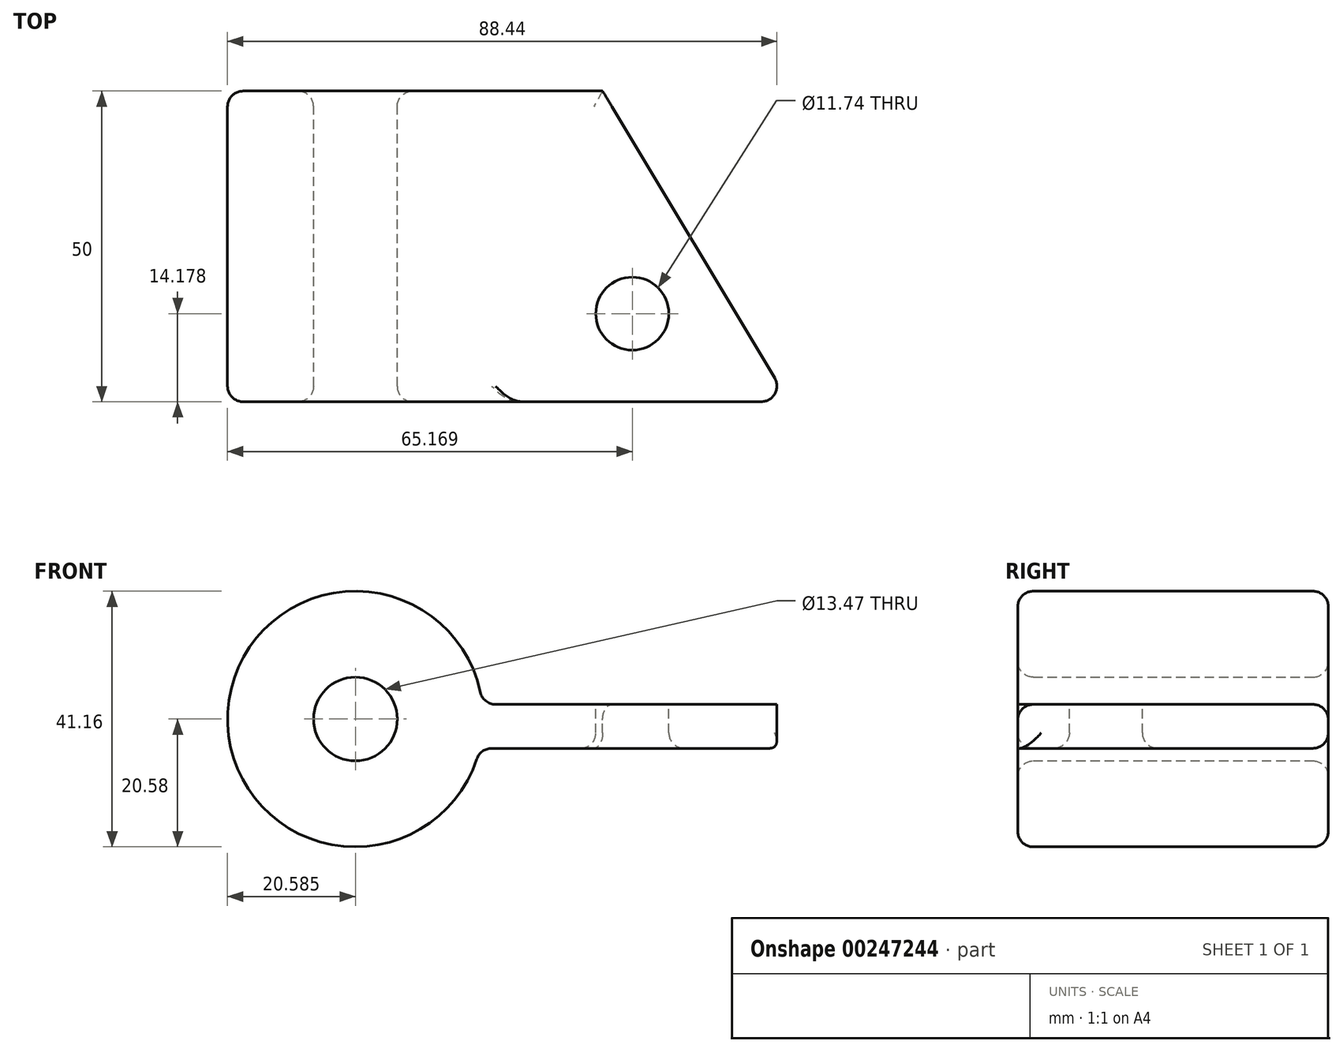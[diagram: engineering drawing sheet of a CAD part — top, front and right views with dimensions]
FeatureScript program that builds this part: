
annotation { "Feature Type Name" : "Feature", "Feature Type Description" : "" }
export const myFeature = defineFeature(function(context is Context, id is Id, definition is map)
    precondition{}
    {
        {
            var Q0;
            Q0=qCreatedBy(makeId("Front.planeOp"),FACE);
            var sketch = newSketch(context, id + "F0", { "sketchPlane" : qUnion([Q0])});
            skCircle(sketch, "E0", {"center": v(-44.76, 6.82) * mm, "radius": 20.58 * mm});
            skCircle(sketch, "E1", {"center": v(-44.76, 6.82) * mm, "radius": 6.74 * mm});
            skSolve(sketch);
        }
        {
            var Q0;
            Q0=makeQuery(id+"F0.imprint","IMPRINT",FACE,{"disambiguationData":[TD([[makeQuery(id+"F0.imprint","IMPRINT",EDGE,{"derivedFrom":sQuery(id+"F0.wireOp",EDGE,"E0")}),1.0]])]});
            extrude(context, id + "F1", {"entities" : qUnion([Q0]), "depth" : 50 * mm});
        }
        {
            var Q0;
            Q0=qCreatedBy(makeId("Right.planeOp"),FACE);
            var sketch = newSketch(context, id + "F2", { "sketchPlane" : qUnion([Q0])});
            skLineSegment(sketch, "E2.bottom", {"start": v(-50.14, 9.18) * mm, "end": v(0, 9.18) * mm});
            skLineSegment(sketch, "E2.top", {"start": v(-50.14, 2.1) * mm, "end": v(0, 2.1) * mm});
            skLineSegment(sketch, "E2.left", {"start": v(-50.14, 9.18) * mm, "end": v(-50.14, 2.1) * mm});
            skLineSegment(sketch, "E2.right", {"start": v(0, 9.18) * mm, "end": v(0, 2.1) * mm});
            skSolve(sketch);
        }
        {
            var Q0;
            Q0=makeQuery(id+"F2.imprint","IMPRINT",FACE,{"disambiguationData":[TD([[makeQuery(id+"F2.imprint","IMPRINT",EDGE,{"derivedFrom":sQuery(id+"F2.wireOp",EDGE,"E2.bottom")}),-1.0]])]});
            extrude(context, id + "F3", {"entities" : qUnion([Q0]), "oppositeDirection" : true, "depth" : 25 * mm});
        }
        {
            var Q0;
            Q0=makeQuery(id+"F3.opExtrude","SWEPT_BODY",BODY,{"disambiguationData":[OSD([sQuery(id+"F2.wireOp",EDGE,"E2.bottom"),sQuery(id+"F2.wireOp",EDGE,"E2.top"),sQuery(id+"F2.wireOp",EDGE,"E2.left"),sQuery(id+"F2.wireOp",EDGE,"E2.right")])]});
            var Q1;
            Q1=makeQuery(id+"F1.opExtrude","SWEPT_BODY",BODY,{"disambiguationData":[OSD([sQuery(id+"F0.wireOp",EDGE,"E0"),sQuery(id+"F0.wireOp",EDGE,"E1")])]});
            booleanBodies(context, id + "F4", {"operationType" : BooleanOperationType.UNION, "tools" : qUnion([Q0, Q1])});
        }
        {
            var Q0;
            Q0=makeQuery(id+"F3.opExtrude","CAP_FACE",FACE,{"disambiguationData":[OSD([sQuery(id+"F2.wireOp",EDGE,"E2.bottom"),sQuery(id+"F2.wireOp",EDGE,"E2.top"),sQuery(id+"F2.wireOp",EDGE,"E2.left"),sQuery(id+"F2.wireOp",EDGE,"E2.right")])],"isStart":true});
            extrude(context, id + "F5", {"entities" : qUnion([Q0]), "operationType" : NewBodyOperationType.ADD, "depth" : 25 * mm});
        }
        {
            var Q0;
            {var subQ0=sQuery(id+"F2.wireOp",EDGE,"E2.left");Q0=makeQuery(id+"F5.boolean.opBoolean","MERGE",FACE,{"derivedFrom":[makeQuery(id+"F3.opExtrude","SWEPT_FACE",FACE,{"disambiguationData":[OSD([subQ0])]}),makeQuery(id+"F5.opExtrude","SWEPT_FACE",FACE,{"disambiguationData":[OSD([subQ0])]})]});}
            var Q1;
            Q1=makeQuery(id+"F1.opExtrude","CAP_FACE",FACE,{"disambiguationData":[OSD([sQuery(id+"F0.wireOp",EDGE,"E0"),sQuery(id+"F0.wireOp",EDGE,"E1")])],"isStart":false});
            extrude(context, id + "F6", {"entities" : qUnion([Q0]), "operationType" : NewBodyOperationType.REMOVE, "endBound" : BoundingType.UP_TO_SURFACE, "oppositeDirection" : true, "endBoundEntityFace" : qUnion([Q1]), "depth" : 25 * mm});
        }
        {
            var Q0;
            {var subQ0=sQuery(id+"F2.wireOp",EDGE,"E2.bottom");Q0=makeQuery(id+"F5.boolean.opBoolean","MERGE",FACE,{"derivedFrom":[makeQuery(id+"F3.opExtrude","SWEPT_FACE",FACE,{"disambiguationData":[OSD([subQ0])]}),makeQuery(id+"F5.opExtrude","SWEPT_FACE",FACE,{"disambiguationData":[OSD([subQ0])]})]});}
            var sketch = newSketch(context, id + "F7", { "sketchPlane" : qUnion([Q0])});
            skLineSegment(sketch, "E3", {"start": v(25, -50) * mm, "end": v(-4.96, 0) * mm});
            skSolve(sketch);
        }
        {
            var Q0;
            {var subQ3=sQuery(id+"F7.wireOp",EDGE,"E3");Q0=makeQuery(id+"F7.imprint","IMPRINT",FACE,{"disambiguationData":[TD([[makeQuery(id+"F7.imprint","IMPRINT",EDGE,{"derivedFrom":subQ3}),-1.0]])]});}
            extrude(context, id + "F8", {"entities" : qUnion([Q0]), "operationType" : NewBodyOperationType.REMOVE, "endBound" : BoundingType.THROUGH_ALL, "oppositeDirection" : true, "depth" : 25 * mm});
        }
        {
            var Q0;
            {var subQ0=sQuery(id+"F2.wireOp",EDGE,"E2.bottom");Q0=makeQuery(id+"F5.boolean.opBoolean","MERGE",FACE,{"derivedFrom":[makeQuery(id+"F3.opExtrude","SWEPT_FACE",FACE,{"disambiguationData":[OSD([subQ0])]}),makeQuery(id+"F5.opExtrude","SWEPT_FACE",FACE,{"disambiguationData":[OSD([subQ0])]})]});}
            var sketch = newSketch(context, id + "F9", { "sketchPlane" : qUnion([Q0])});
            skCircle(sketch, "E4", {"center": v(-0.18, -35.82) * mm, "radius": 5.87 * mm});
            skSolve(sketch);
        }
        {
            var Q0;
            Q0=makeQuery(id+"F9.imprint","IMPRINT",FACE,{"disambiguationData":[TD([[makeQuery(id+"F9.imprint","IMPRINT",EDGE,{"derivedFrom":sQuery(id+"F9.wireOp",EDGE,"E4")}),1.0]])]});
            extrude(context, id + "F10", {"entities" : qUnion([Q0]), "operationType" : NewBodyOperationType.REMOVE, "endBound" : BoundingType.THROUGH_ALL, "oppositeDirection" : true, "depth" : 25 * mm});
        }
        {
            var Q0;
            Q0=makeQuery(id+"F10.boolean.opBoolean","COPY",EDGE,{"derivedFrom":makeQuery(id+"F10.opExtrude","CAP_EDGE",EDGE,{"disambiguationData":[OSD([sQuery(id+"F9.wireOp",EDGE,"E4")])],"isStart":true})});
            var Q1;
            Q1=makeQuery(id+"F6.boolean.opBoolean","COPY",EDGE,{"derivedFrom":makeQuery(id+"F6.opExtrude","CAP_EDGE",EDGE,{"disambiguationData":[OSD([sQuery(id+"F2.wireOp",EDGE,"E2.bottom"),sQuery(id+"F2.wireOp",EDGE,"E2.left")])],"isStart":false})});
            var Q2;
            Q2=makeQuery(id+"F6.boolean.opBoolean","COPY",EDGE,{"derivedFrom":makeQuery(id+"F6.opExtrude","CAP_EDGE",EDGE,{"disambiguationData":[OSD([sQuery(id+"F2.wireOp",EDGE,"E2.top"),sQuery(id+"F2.wireOp",EDGE,"E2.left")])],"isStart":false})});
            var Q3;
            Q3=makeQuery(id+"F1.opExtrude","CAP_EDGE",EDGE,{"disambiguationData":[OSD([sQuery(id+"F0.wireOp",EDGE,"E0")])],"isStart":false});
            var Q4;
            {var subQ0=sQuery(id+"F2.wireOp",EDGE,"E2.right");var subQ1=sQuery(id+"F2.wireOp",EDGE,"E2.bottom");Q4=makeQuery(id+"F5.boolean.opBoolean","MERGE",EDGE,{"derivedFrom":[makeQuery(id+"F3.opExtrude","SWEPT_EDGE",EDGE,{"disambiguationData":[OSD([subQ1,subQ0])]}),makeQuery(id+"F5.opExtrude","SWEPT_EDGE",EDGE,{"disambiguationData":[OSD([subQ1,subQ0])]})]});}
            var Q5;
            Q5=makeQuery(id+"F1.opExtrude","CAP_EDGE",EDGE,{"disambiguationData":[OSD([sQuery(id+"F0.wireOp",EDGE,"E1")])],"isStart":false});
            var Q6;
            Q6=makeQuery(id+"F4.opBoolean","INTERSECT",EDGE,{"derivedFrom":[makeQuery(id+"F1.opExtrude","SWEPT_FACE",FACE,{"disambiguationData":[OSD([sQuery(id+"F0.wireOp",EDGE,"E0")])]}),makeQuery(id+"F3.opExtrude","SWEPT_FACE",FACE,{"disambiguationData":[OSD([sQuery(id+"F2.wireOp",EDGE,"E2.bottom")])]})]});
            var Q7;
            Q7=makeQuery(id+"F1.opExtrude","CAP_EDGE",EDGE,{"disambiguationData":[OSD([sQuery(id+"F0.wireOp",EDGE,"E0")])],"isStart":true});
            var Q8;
            Q8=makeQuery(id+"F8.boolean.opBoolean","COPY",EDGE,{"derivedFrom":makeQuery(id+"F8.opExtrude","CAP_EDGE",EDGE,{"disambiguationData":[OSD([sQuery(id+"F7.wireOp",EDGE,"E3")])],"isStart":true})});
            var Q9;
            {var subQ0=sQuery(id+"F2.wireOp",EDGE,"E2.top");Q9=makeQuery(id+"F10.boolean.opBoolean","INTERSECT",EDGE,{"derivedFrom":[makeQuery(id+"F5.boolean.opBoolean","MERGE",FACE,{"derivedFrom":[makeQuery(id+"F3.opExtrude","SWEPT_FACE",FACE,{"disambiguationData":[OSD([subQ0])]}),makeQuery(id+"F5.opExtrude","SWEPT_FACE",FACE,{"disambiguationData":[OSD([subQ0])]})]}),makeQuery(id+"F10.opExtrude","SWEPT_FACE",FACE,{"disambiguationData":[OSD([sQuery(id+"F9.wireOp",EDGE,"E4")])]})]});}
            var Q10;
            {var subQ0=sQuery(id+"F2.wireOp",EDGE,"E2.right");var subQ1=sQuery(id+"F2.wireOp",EDGE,"E2.top");Q10=makeQuery(id+"F5.boolean.opBoolean","MERGE",EDGE,{"derivedFrom":[makeQuery(id+"F3.opExtrude","SWEPT_EDGE",EDGE,{"disambiguationData":[OSD([subQ1,subQ0])]}),makeQuery(id+"F5.opExtrude","SWEPT_EDGE",EDGE,{"disambiguationData":[OSD([subQ1,subQ0])]})]});}
            var Q11;
            Q11=makeQuery(id+"F1.opExtrude","CAP_EDGE",EDGE,{"disambiguationData":[OSD([sQuery(id+"F0.wireOp",EDGE,"E1")])],"isStart":true});
            var Q12;
            {var subQ0=sQuery(id+"F2.wireOp",EDGE,"E2.top");Q12=makeQuery(id+"F8.boolean.opBoolean","INTERSECT",EDGE,{"derivedFrom":[makeQuery(id+"F5.boolean.opBoolean","MERGE",FACE,{"derivedFrom":[makeQuery(id+"F3.opExtrude","SWEPT_FACE",FACE,{"disambiguationData":[OSD([subQ0])]}),makeQuery(id+"F5.opExtrude","SWEPT_FACE",FACE,{"disambiguationData":[OSD([subQ0])]})]}),makeQuery(id+"F8.opExtrude","SWEPT_FACE",FACE,{"disambiguationData":[OSD([sQuery(id+"F7.wireOp",EDGE,"E3")])]})]});}
            var Q13;
            Q13=makeQuery(id+"F4.opBoolean","INTERSECT",EDGE,{"derivedFrom":[makeQuery(id+"F1.opExtrude","SWEPT_FACE",FACE,{"disambiguationData":[OSD([sQuery(id+"F0.wireOp",EDGE,"E0")])]}),makeQuery(id+"F3.opExtrude","SWEPT_FACE",FACE,{"disambiguationData":[OSD([sQuery(id+"F2.wireOp",EDGE,"E2.top")])]})]});
            var Q14;
            Q14=makeQuery(id+"F8.boolean.opBoolean","COPY",EDGE,{"derivedFrom":makeQuery(id+"F8.opExtrude","SWEPT_EDGE",EDGE,{"disambiguationData":[OSD([sQuery(id+"F2.wireOp",EDGE,"E2.bottom"),sQuery(id+"F2.wireOp",EDGE,"E2.right"),sQuery(id+"F7.wireOp",EDGE,"E3")])]})});
            var Q15;
            {var subQ0=sQuery(id+"F2.wireOp",EDGE,"E2.left");Q15=makeQuery(id+"F8.boolean.opBoolean","MERGE",EDGE,{"derivedFrom":[makeQuery(id+"F6.boolean.opBoolean","COPY",EDGE,{"derivedFrom":makeQuery(id+"F6.opExtrude","CAP_EDGE",EDGE,{"disambiguationData":[OSD([subQ0]),TDD([makeQuery(id+"F5.opExtrude","CAP_EDGE",EDGE,{"disambiguationData":[OSD([subQ0])],"isStart":false})])],"isStart":false})})],"fromTools":[makeQuery(id+"F8.opExtrude","SWEPT_EDGE",EDGE,{"disambiguationData":[OSD([sQuery(id+"F2.wireOp",EDGE,"E2.bottom"),subQ0,sQuery(id+"F7.wireOp",EDGE,"E3")])]})]});}
            fillet(context, id + "F11", {"entities" : qUnion([Q0, Q1, Q2, Q3, Q4, Q5, Q6, Q7, Q8, Q9, Q10, Q11, Q12, Q13, Q14, Q15]), "radius" : 2.5 * mm, "tangentPropagation" : true, "allowEdgeOverflow" : false});
        }
    });
